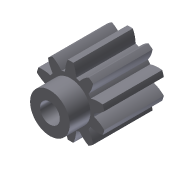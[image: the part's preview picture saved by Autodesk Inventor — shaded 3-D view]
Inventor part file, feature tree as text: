
AUTODESK INVENTOR PART (.ipt)
format: ipt  version: 2013 (Build 170138000, 138)  size: 186,880 bytes
history: native  units: mm (DEFAULTED — no unit token found)
features: sketch x4, extrude x3, plane x3, other x3
ambient origin geometry x8: Origin, YZ Plane, XZ Plane, XY Plane, X Axis, Y Axis, Z Axis, Center Point
bodies: Solid1 (feature_tree)
feature tree (13):
  extrude  "Extrusion1"  Depth=9.525mm TaperAngle=0.0deg
  plane  "Work Plane1"
  plane  "Work Plane2"
  plane  "Work Plane3"
  other  "Spur Gear"
  extrude  "Extrusion2"  Depth=76.2mm TaperAngle=0.0deg
  extrude  "Extrusion3"  TaperAngle=0.0deg  [1 undecoded]
  sketch  "Sketch1"  dims[d0=11.1125mm d1=9.525mm d2=0.0mm]
  sketch  "Sketch2"  dims[d3=9.525mm d4=76.2mm d5=0.0mm]
  other  "Srf1"
  sketch  "Sketch3"  dims[d6=0.0mm d7=3.141593mm d9=0.0mm]
  sketch  "Sketch4"  dims[d14=0.0mm d15=9.525mm d16=0.0mm d17=0.0mm d18=0.0mm d19=9.525mm d20=3.175mm d21=6.35mm d22=3.302mm d23=0.0mm d24=3.175mm d25=3.302mm d26=0.0mm]
  other  "Pitch Diameter"
note: 1 required parameter value undecoded (feature->parameter linkage not recoverable at this tier; creation-order binding heuristic only, values carry confidence <= 0.55)
